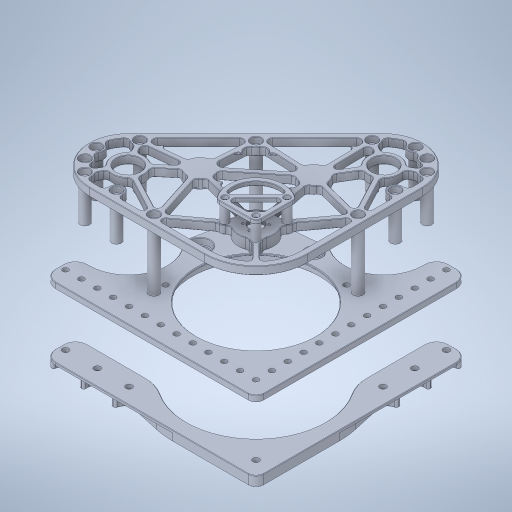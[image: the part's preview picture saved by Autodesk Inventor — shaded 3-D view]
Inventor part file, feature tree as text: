
AUTODESK INVENTOR PART (.ipt)
format: ipt  version: 2023.3 (Build 273359000, 359)  size: 1,677,824 bytes
history: native  units: in
note: dims shown in document units (in); Inventor stores cm internally (conversion verified against a paired STEP export)
features: other x14, chamfer x4
ambient origin geometry x8: Origin, YZ Plane, XZ Plane, XY Plane, X Axis, Y Axis, Z Axis, Center Point
bodies: Solid1 (feature_tree), Solid2 (feature_tree), Solid3 (feature_tree), Solid4 (feature_tree), Solid5 (feature_tree), Solid6 (feature_tree), Solid7 (feature_tree), Solid8 (feature_tree), Solid9 (feature_tree), Solid10 (feature_tree), Solid11 (feature_tree), Solid13 (feature_tree), Solid14 (feature_tree), Solid15 (feature_tree), Solid16 (feature_tree), Solid17 (feature_tree), Solid18 (feature_tree), Solid19 (feature_tree)
feature tree (18):
  other  "Boss-Extrude4[1]"
  other  "Boss-Extrude4[2]"
  other  "Boss-Extrude4[3]"
  other  "Boss-Extrude6[1]"
  other  "Boss-Extrude6[2]"
  other  "Boss-Extrude6[3]"
  other  "Boss-Extrude6[4]"
  other  "Boss-Extrude6[5]"
  other  "Boss-Extrude6[6]"
  other  "Boss-Extrude6[7]"
  other  "Boss-Extrude6[8]"
  other  "Boss-Extrude17[1]"
  other  "Boss-Extrude17[2]"
  other  "Boss-Extrude17[3]"
  chamfer  "Chamfer4"  [1 undecoded]
  chamfer  "Chamfer1"  [1 undecoded]
  chamfer  "Chamfer3"  [1 undecoded]
  chamfer  "Chamfer2"  [1 undecoded]
note: 4 required parameter values undecoded (feature->parameter linkage not recoverable at this tier; creation-order binding heuristic only, values carry confidence <= 0.55)
